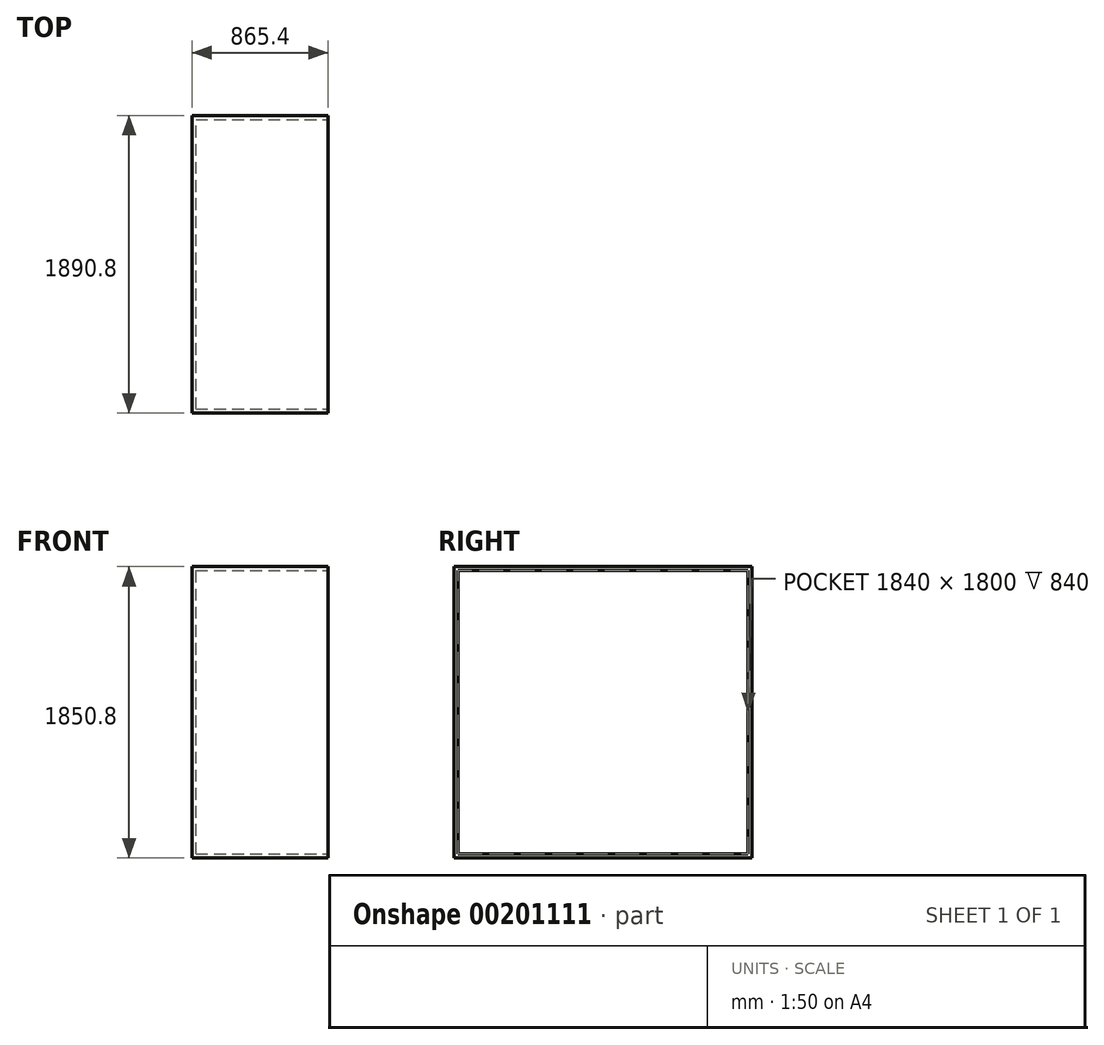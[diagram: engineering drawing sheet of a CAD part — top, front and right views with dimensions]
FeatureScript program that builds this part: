
annotation { "Feature Type Name" : "Feature", "Feature Type Description" : "" }
export const myFeature = defineFeature(function(context is Context, id is Id, definition is map)
    precondition{}
    {
        {
            var Q0;
            Q0=qCreatedBy(makeId("Top.planeOp"),FACE);
            var sketch = newSketch(context, id + "F0", { "sketchPlane" : qUnion([Q0])});
            skLineSegment(sketch, "E0.bottom", {"start": v(-420, -920) * mm, "end": v(420, -920) * mm});
            skLineSegment(sketch, "E0.top", {"start": v(-420, 920) * mm, "end": v(420, 920) * mm});
            skLineSegment(sketch, "E0.left", {"start": v(-420, -920) * mm, "end": v(-420, 920) * mm});
            skLineSegment(sketch, "E0.right", {"start": v(420, -920) * mm, "end": v(420, 920) * mm});
            skPoint(sketch, "E0.middle", {"position": v(0, 0) * mm});
            skSolve(sketch);
        }
        {
            var Q0;
            Q0 = qSketchRegion(id + "F0", true);
            extrude(context, id + "F1", {"entities" : qUnion([Q0]), "oppositeDirection" : true, "depth" : 1800 * mm});
        }
        {
            var Q0;
            Q0=makeQuery(id+"F1.opExtrude","SWEPT_FACE",FACE,{"disambiguationData":[OSD([sQuery(id+"F0.wireOp",EDGE,"E0.right")])]});
            shell(context, id + "F2", {"entities" : qUnion([Q0]), "thickness" : 25.4 * mm, "oppositeDirection" : true});
        }
    });
